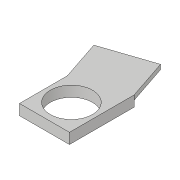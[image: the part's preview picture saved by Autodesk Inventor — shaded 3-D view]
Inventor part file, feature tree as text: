
AUTODESK INVENTOR PART (.ipt)
format: ipt  version: 2018.3 (Build 223284000, 284)  size: 119,808 bytes
history: native  units: in
note: dims shown in document units (in); Inventor stores cm internally (conversion verified against a paired STEP export)
features: extrude x2, sketch x1
ambient origin geometry x8: Origin, YZ Plane, XZ Plane, XY Plane, X Axis, Y Axis, Z Axis, Center Point
bodies: Solid1 (feature_tree)
feature tree (3):
  extrude  "Extrusion1"  Depth=0.1105in
  extrude  "Extrusion2"  Depth=1.1003in
  sketch  "Sketch1"  dims[d0=0.75in d1=0.875in d2=1.1003in d3=1.0432in d4=0.88in d5=0.221in d6=0.0in d7=0.125in d8=0.0in d18=0.5216in d20=1.1095in d24=0.1105in d26=0.5625in d27=0.119in d28=1.0in d29=1.3499in]
